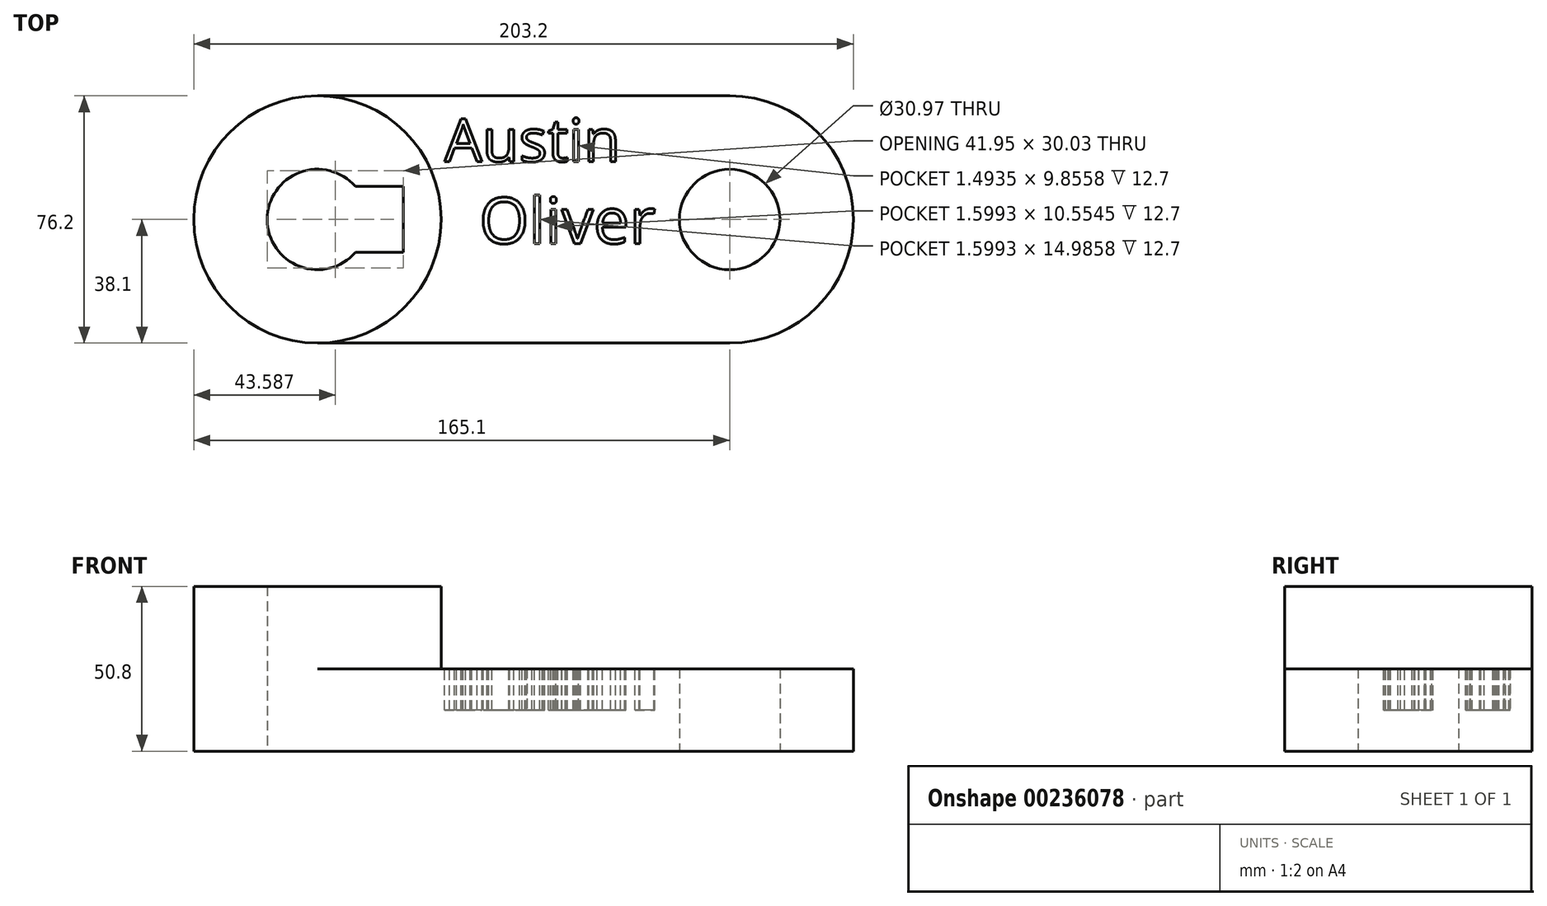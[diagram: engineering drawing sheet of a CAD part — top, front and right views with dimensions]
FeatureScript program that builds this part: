
annotation { "Feature Type Name" : "Feature", "Feature Type Description" : "" }
export const myFeature = defineFeature(function(context is Context, id is Id, definition is map)
    precondition{}
    {
        {
            var Q0;
            Q0=qCreatedBy(makeId("Top.planeOp"),FACE);
            var sketch = newSketch(context, id + "F0", { "sketchPlane" : qUnion([Q0])});
            skCircle(sketch, "E0", {"center": v(0, 0) * mm, "radius": 38.1 * mm});
            skCircle(sketch, "E1", {"center": v(127, 0) * mm, "radius": 38.1 * mm});
            skLineSegment(sketch, "E2", {"start": v(127, -38.1) * mm, "end": v(0, -38.1) * mm});
            skLineSegment(sketch, "E3", {"start": v(127, 38.1) * mm, "end": v(0, 38.1) * mm});
            skArc(sketch, "E4", {"start": v(11.67, 10.18) * mm, "mid": v(-15.49, 0) * mm, "end": v(11.67, -10.18) * mm});
            skCircle(sketch, "E5", {"center": v(127, 0) * mm, "radius": 15.49 * mm});
            skLineSegment(sketch, "E6.bottom", {"start": v(11.67, 10.18) * mm, "end": v(26.46, 10.18) * mm});
            skLineSegment(sketch, "E6.top", {"start": v(11.67, -10.18) * mm, "end": v(26.46, -10.18) * mm});
            skLineSegment(sketch, "E6.right", {"start": v(26.46, 10.18) * mm, "end": v(26.46, -10.18) * mm});
            skSolve(sketch);
        }
        {
            var Q0;
            {var subQ0=sQuery(id+"F0.wireOp",EDGE,"E2");Q0=makeQuery(id+"F0.imprint","IMPRINT",FACE,{"disambiguationData":[TD([[makeQuery(id+"F0.imprint","IMPRINT",EDGE,{"derivedFrom":subQ0}),-1.0]])]});}
            var Q1;
            Q1=makeQuery(id+"F0.imprint","IMPRINT",FACE,{"disambiguationData":[TD([[makeQuery(id+"F0.imprint","IMPRINT",EDGE,{"derivedFrom":sQuery(id+"F0.wireOp",EDGE,"E5")}),-1.0]])]});
            extrude(context, id + "F1", {"entities" : qUnion([Q0, Q1]), "depth" : 25.4 * mm});
        }
        {
            var Q0;
            Q0=makeQuery(id+"F0.imprint","IMPRINT",FACE,{"disambiguationData":[TD([[makeQuery(id+"F0.imprint","IMPRINT",EDGE,{"derivedFrom":sQuery(id+"F0.wireOp",EDGE,"E4")}),-1.0]])]});
            extrude(context, id + "F2", {"entities" : qUnion([Q0]), "operationType" : NewBodyOperationType.ADD, "depth" : 50.8 * mm});
        }
        {
            var Q0;
            Q0=makeQuery(id+"F1.opExtrude","CAP_FACE",FACE,{"disambiguationData":[OSD([sQuery(id+"F0.wireOp",EDGE,"E0"),sQuery(id+"F0.wireOp",EDGE,"E1"),sQuery(id+"F0.wireOp",EDGE,"E2"),sQuery(id+"F0.wireOp",EDGE,"E3"),sQuery(id+"F0.wireOp",EDGE,"E5")])],"isStart":false});
            var sketch = newSketch(context, id + "F3", { "sketchPlane" : qUnion([Q0])});
            skText(sketch, "E7", { "text": "Austin", "fontName": "OpenSans-Regular.ttf"});
            skText(sketch, "E8", { "text": "Oliver", "fontName": "OpenSans-Regular.ttf"});
            const initialGuessF3  = {"E7": [0.03908, 0.01783, 1, 0, 0.01326], "E8": [0.04982, -0.00742, 1, 0, 0.0142]};
            skSetInitialGuess(sketch, initialGuessF3);
            skSolve(sketch);
        }
        {
            var Q0;
            Q0 = qSketchRegion(id + "F3", true);
            extrude(context, id + "F4", {"entities" : qUnion([Q0]), "operationType" : NewBodyOperationType.REMOVE, "oppositeDirection" : true, "depth" : 12.7 * mm});
        }
    });
